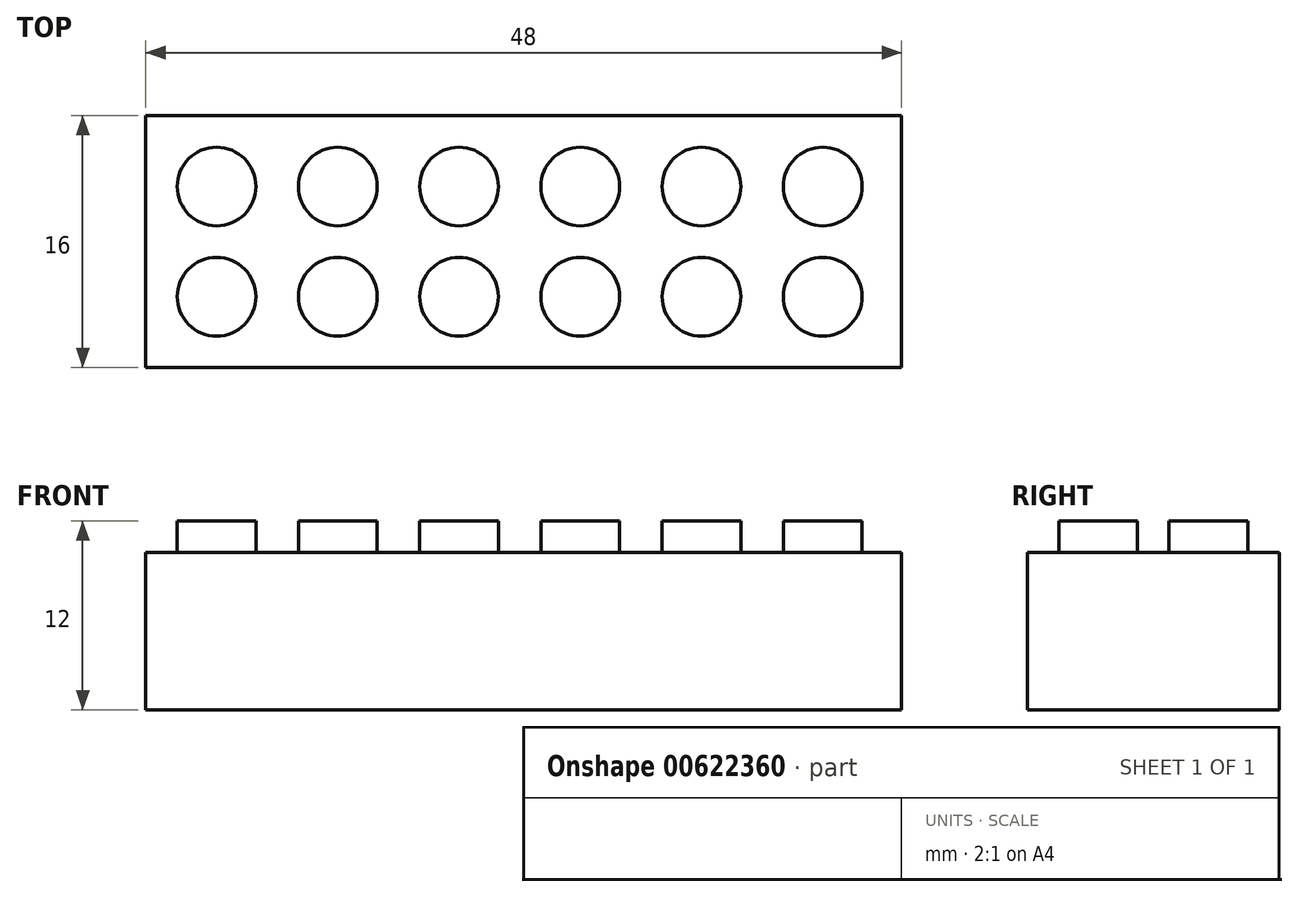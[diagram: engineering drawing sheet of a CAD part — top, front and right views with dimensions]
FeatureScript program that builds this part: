
annotation { "Feature Type Name" : "Feature", "Feature Type Description" : "" }
export const myFeature = defineFeature(function(context is Context, id is Id, definition is map)
    precondition{}
    {
        {
            var Q0;
            Q0=qCreatedBy(makeId("Top.planeOp"),FACE);
            var sketch = newSketch(context, id + "F0", { "sketchPlane" : qUnion([Q0])});
            skLineSegment(sketch, "E0.bottom", {"start": v(-51.65, 11.37) * mm, "end": v(-3.65, 11.37) * mm});
            skLineSegment(sketch, "E0.top", {"start": v(-51.65, 27.37) * mm, "end": v(-3.65, 27.37) * mm});
            skLineSegment(sketch, "E0.left", {"start": v(-51.65, 11.37) * mm, "end": v(-51.65, 27.37) * mm});
            skLineSegment(sketch, "E0.right", {"start": v(-3.65, 11.37) * mm, "end": v(-3.65, 27.37) * mm});
            skSolve(sketch);
        }
        {
            var Q0;
            Q0=makeQuery(id+"F0.imprint","IMPRINT",FACE,{"disambiguationData":[TD([[makeQuery(id+"F0.imprint","IMPRINT",EDGE,{"derivedFrom":sQuery(id+"F0.wireOp",EDGE,"E0.bottom")}),1.0]])]});
            extrude(context, id + "F1", {"entities" : qUnion([Q0]), "depth" : 10 * mm, "offsetDistance" : 25 * mm});
        }
        {
            var Q0;
            Q0=makeQuery(id+"F1.opExtrude","CAP_FACE",FACE,{"disambiguationData":[OSD([sQuery(id+"F0.wireOp",EDGE,"E0.bottom"),sQuery(id+"F0.wireOp",EDGE,"E0.top"),sQuery(id+"F0.wireOp",EDGE,"E0.left"),sQuery(id+"F0.wireOp",EDGE,"E0.right")])],"isStart":false});
            var sketch = newSketch(context, id + "F2", { "sketchPlane" : qUnion([Q0])});
            skCircle(sketch, "E1", {"center": v(-47.15, 22.87) * mm, "radius": 2.5 * mm});
            skCircle(sketch, "E2.0.1.0", {"center": v(-47.15, 15.87) * mm, "radius": 2.5 * mm});
            skCircle(sketch, "E2.1.0.0", {"center": v(-39.45, 22.87) * mm, "radius": 2.5 * mm});
            skCircle(sketch, "E2.1.1.0", {"center": v(-39.45, 15.87) * mm, "radius": 2.5 * mm});
            skCircle(sketch, "E2.2.0.0", {"center": v(-31.75, 22.87) * mm, "radius": 2.5 * mm});
            skCircle(sketch, "E2.2.1.0", {"center": v(-31.75, 15.87) * mm, "radius": 2.5 * mm});
            skCircle(sketch, "E2.3.0.0", {"center": v(-24.05, 22.87) * mm, "radius": 2.5 * mm});
            skCircle(sketch, "E2.3.1.0", {"center": v(-24.05, 15.87) * mm, "radius": 2.5 * mm});
            skCircle(sketch, "E2.4.0.0", {"center": v(-16.35, 22.87) * mm, "radius": 2.5 * mm});
            skCircle(sketch, "E2.4.1.0", {"center": v(-16.35, 15.87) * mm, "radius": 2.5 * mm});
            skCircle(sketch, "E2.5.0.0", {"center": v(-8.65, 22.87) * mm, "radius": 2.5 * mm});
            skCircle(sketch, "E2.5.1.0", {"center": v(-8.65, 15.87) * mm, "radius": 2.5 * mm});
            skLineSegment(sketch, "E2.direction1", {"start": v(-47.15, 22.87) * mm, "end": v(-39.45, 22.87) * mm, "construction": true});
            skLineSegment(sketch, "E2.direction2", {"start": v(-47.15, 22.87) * mm, "end": v(-47.15, 15.87) * mm, "construction": true});
            skSolve(sketch);
        }
        {
            var Q0;
            Q0=makeQuery(id+"F2.imprint","IMPRINT",FACE,{"disambiguationData":[TD([[makeQuery(id+"F2.imprint","IMPRINT",EDGE,{"derivedFrom":sQuery(id+"F2.wireOp",EDGE,"E1")}),1.0]])]});
            var Q1;
            Q1=makeQuery(id+"F2.imprint","IMPRINT",FACE,{"disambiguationData":[TD([[makeQuery(id+"F2.imprint","IMPRINT",EDGE,{"derivedFrom":sQuery(id+"F2.wireOp",EDGE,"E2.0.1.0")}),1.0]])]});
            var Q2;
            Q2=makeQuery(id+"F2.imprint","IMPRINT",FACE,{"disambiguationData":[TD([[makeQuery(id+"F2.imprint","IMPRINT",EDGE,{"derivedFrom":sQuery(id+"F2.wireOp",EDGE,"E2.1.1.0")}),1.0]])]});
            var Q3;
            Q3=makeQuery(id+"F2.imprint","IMPRINT",FACE,{"disambiguationData":[TD([[makeQuery(id+"F2.imprint","IMPRINT",EDGE,{"derivedFrom":sQuery(id+"F2.wireOp",EDGE,"E2.1.0.0")}),1.0]])]});
            var Q4;
            Q4=makeQuery(id+"F2.imprint","IMPRINT",FACE,{"disambiguationData":[TD([[makeQuery(id+"F2.imprint","IMPRINT",EDGE,{"derivedFrom":sQuery(id+"F2.wireOp",EDGE,"E2.2.0.0")}),1.0]])]});
            var Q5;
            Q5=makeQuery(id+"F2.imprint","IMPRINT",FACE,{"disambiguationData":[TD([[makeQuery(id+"F2.imprint","IMPRINT",EDGE,{"derivedFrom":sQuery(id+"F2.wireOp",EDGE,"E2.3.0.0")}),1.0]])]});
            var Q6;
            Q6=makeQuery(id+"F2.imprint","IMPRINT",FACE,{"disambiguationData":[TD([[makeQuery(id+"F2.imprint","IMPRINT",EDGE,{"derivedFrom":sQuery(id+"F2.wireOp",EDGE,"E2.4.0.0")}),1.0]])]});
            var Q7;
            Q7=makeQuery(id+"F2.imprint","IMPRINT",FACE,{"disambiguationData":[TD([[makeQuery(id+"F2.imprint","IMPRINT",EDGE,{"derivedFrom":sQuery(id+"F2.wireOp",EDGE,"E2.5.0.0")}),1.0]])]});
            var Q8;
            Q8=makeQuery(id+"F2.imprint","IMPRINT",FACE,{"disambiguationData":[TD([[makeQuery(id+"F2.imprint","IMPRINT",EDGE,{"derivedFrom":sQuery(id+"F2.wireOp",EDGE,"E2.5.1.0")}),1.0]])]});
            var Q9;
            Q9=makeQuery(id+"F2.imprint","IMPRINT",FACE,{"disambiguationData":[TD([[makeQuery(id+"F2.imprint","IMPRINT",EDGE,{"derivedFrom":sQuery(id+"F2.wireOp",EDGE,"E2.4.1.0")}),1.0]])]});
            var Q10;
            Q10=makeQuery(id+"F2.imprint","IMPRINT",FACE,{"disambiguationData":[TD([[makeQuery(id+"F2.imprint","IMPRINT",EDGE,{"derivedFrom":sQuery(id+"F2.wireOp",EDGE,"E2.3.1.0")}),1.0]])]});
            var Q11;
            Q11=makeQuery(id+"F2.imprint","IMPRINT",FACE,{"disambiguationData":[TD([[makeQuery(id+"F2.imprint","IMPRINT",EDGE,{"derivedFrom":sQuery(id+"F2.wireOp",EDGE,"E2.2.1.0")}),1.0]])]});
            extrude(context, id + "F3", {"entities" : qUnion([Q0, Q1, Q2, Q3, Q4, Q5, Q6, Q7, Q8, Q9, Q10, Q11]), "operationType" : NewBodyOperationType.ADD, "depth" : 2 * mm, "offsetDistance" : 25 * mm});
        }
    });
